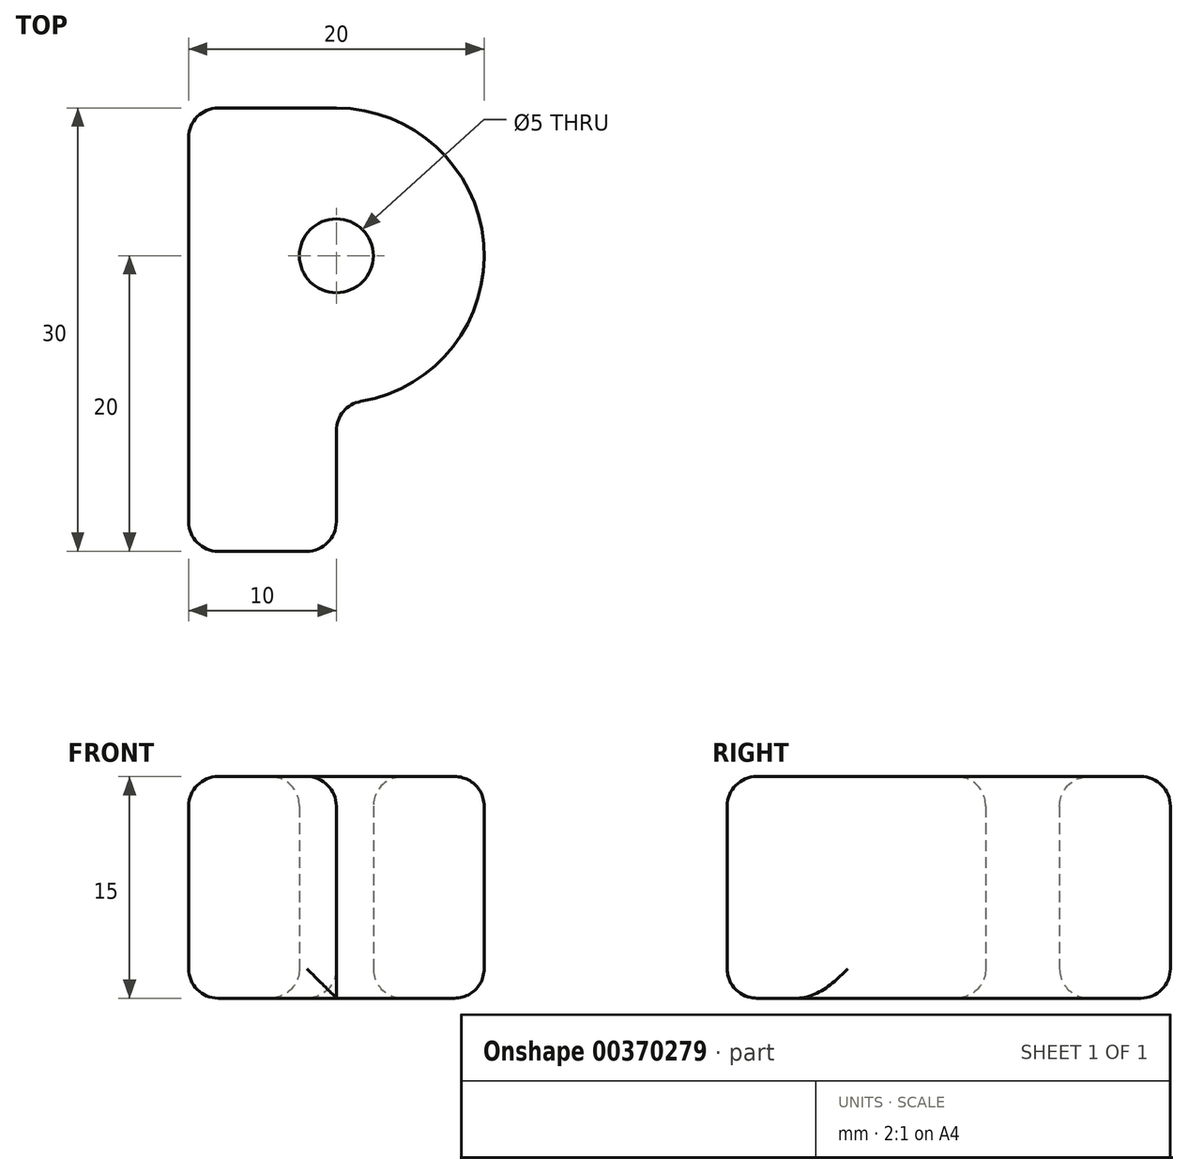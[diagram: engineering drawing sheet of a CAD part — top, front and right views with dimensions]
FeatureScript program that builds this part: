
annotation { "Feature Type Name" : "Feature", "Feature Type Description" : "" }
export const myFeature = defineFeature(function(context is Context, id is Id, definition is map)
    precondition{}
    {
        {
            var Q0;
            Q0=qCreatedBy(makeId("Top.planeOp"),FACE);
            var sketch = newSketch(context, id + "F0", { "sketchPlane" : qUnion([Q0])});
            skLineSegment(sketch, "E0", {"start": v(0, 0) * mm, "end": v(0, 30) * mm});
            skLineSegment(sketch, "E1", {"start": v(0, 30) * mm, "end": v(10, 30) * mm});
            skArc(sketch, "E2", {"start": v(10, 30) * mm, "mid": v(20, 20) * mm, "end": v(10, 10) * mm});
            skLineSegment(sketch, "E3", {"start": v(10, 10) * mm, "end": v(10, 0) * mm});
            skLineSegment(sketch, "E4", {"start": v(10, 0) * mm, "end": v(0, 0) * mm});
            skCircle(sketch, "E5", {"center": v(10, 20) * mm, "radius": 2.5 * mm});
            skSolve(sketch);
        }
        {
            var Q0;
            Q0 = qSketchRegion(id + "F0", true);
            extrude(context, id + "F1", {"entities" : qUnion([Q0]), "depth" : 15 * mm});
        }
        {
            var Q0;
            Q0=makeQuery(id+"F1.opExtrude","CAP_EDGE",EDGE,{"disambiguationData":[OSD([sQuery(id+"F0.wireOp",EDGE,"E4")])],"isStart":false});
            var Q1;
            Q1=makeQuery(id+"F1.opExtrude","CAP_EDGE",EDGE,{"disambiguationData":[OSD([sQuery(id+"F0.wireOp",EDGE,"E3")])],"isStart":false});
            var Q2;
            Q2=makeQuery(id+"F1.opExtrude","CAP_EDGE",EDGE,{"disambiguationData":[OSD([sQuery(id+"F0.wireOp",EDGE,"E2")])],"isStart":false});
            var Q3;
            Q3=makeQuery(id+"F1.opExtrude","CAP_EDGE",EDGE,{"disambiguationData":[OSD([sQuery(id+"F0.wireOp",EDGE,"E0")])],"isStart":false});
            var Q4;
            Q4=makeQuery(id+"F1.opExtrude","CAP_EDGE",EDGE,{"disambiguationData":[OSD([sQuery(id+"F0.wireOp",EDGE,"E0")])],"isStart":true});
            var Q5;
            Q5=makeQuery(id+"F1.opExtrude","SWEPT_FACE",FACE,{"disambiguationData":[OSD([sQuery(id+"F0.wireOp",EDGE,"E2")])]});
            var Q6;
            Q6=makeQuery(id+"F1.opExtrude","CAP_EDGE",EDGE,{"disambiguationData":[OSD([sQuery(id+"F0.wireOp",EDGE,"E5")])],"isStart":true});
            var Q7;
            Q7=makeQuery(id+"F1.opExtrude","CAP_EDGE",EDGE,{"disambiguationData":[OSD([sQuery(id+"F0.wireOp",EDGE,"E4")])],"isStart":true});
            var Q8;
            Q8=makeQuery(id+"F1.opExtrude","SWEPT_FACE",FACE,{"disambiguationData":[OSD([sQuery(id+"F0.wireOp",EDGE,"E4")])]});
            var Q9;
            Q9=makeQuery(id+"F1.opExtrude","SWEPT_EDGE",EDGE,{"disambiguationData":[OSD([sQuery(id+"F0.wireOp",EDGE,"E0"),sQuery(id+"F0.wireOp",EDGE,"E1")])]});
            var Q10;
            Q10=makeQuery(id+"F1.opExtrude","SWEPT_FACE",FACE,{"disambiguationData":[OSD([sQuery(id+"F0.wireOp",EDGE,"E5")])]});
            var Q11;
            Q11=makeQuery(id+"F1.opExtrude","CAP_FACE",FACE,{"disambiguationData":[OSD([sQuery(id+"F0.wireOp",EDGE,"E0"),sQuery(id+"F0.wireOp",EDGE,"E1"),sQuery(id+"F0.wireOp",EDGE,"E2"),sQuery(id+"F0.wireOp",EDGE,"E3"),sQuery(id+"F0.wireOp",EDGE,"E4"),sQuery(id+"F0.wireOp",EDGE,"E5")])],"isStart":false});
            fillet(context, id + "F2", {"entities" : qUnion([Q0, Q1, Q2, Q3, Q4, Q5, Q6, Q7, Q8, Q9, Q10, Q11]), "radius" : 2 * mm, "tangentPropagation" : true, "allowEdgeOverflow" : false});
        }
    });
